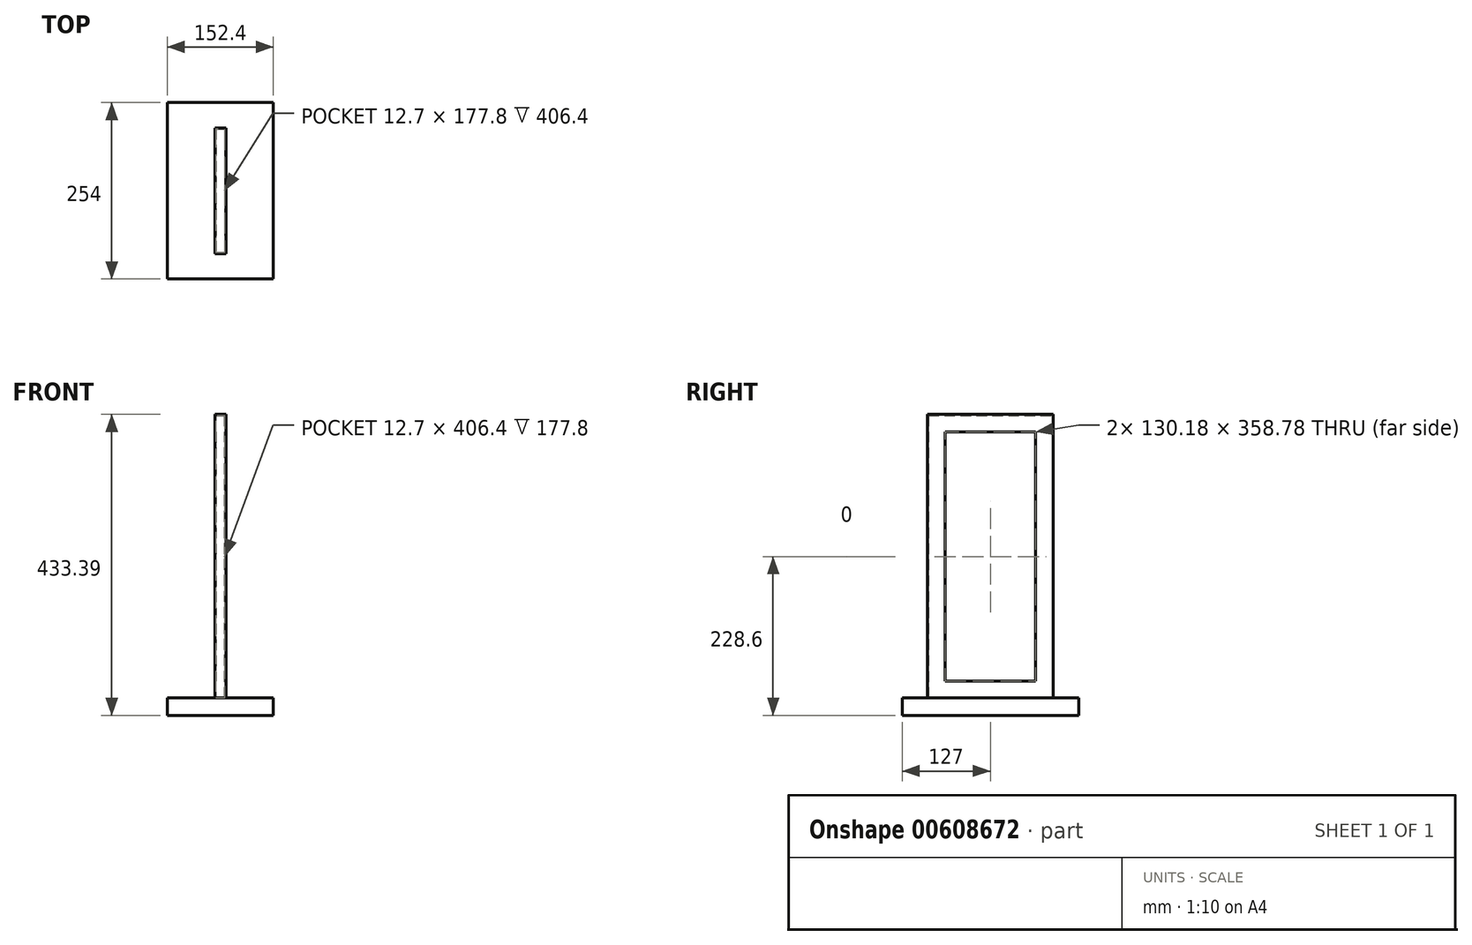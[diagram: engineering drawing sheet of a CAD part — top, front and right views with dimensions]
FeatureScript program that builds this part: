
annotation { "Feature Type Name" : "Feature", "Feature Type Description" : "" }
export const myFeature = defineFeature(function(context is Context, id is Id, definition is map)
    precondition{}
    {
        {
            var Q0;
            Q0=qCreatedBy(makeId("Right.planeOp"),FACE);
            var sketch = newSketch(context, id + "F0", { "sketchPlane" : qUnion([Q0])});
            skPoint(sketch, "E0.middle", {"position": v(0, 228.6) * mm});
            skLineSegment(sketch, "E1.bottom", {"start": v(88.9, 25.4) * mm, "end": v(-88.9, 25.4) * mm});
            skLineSegment(sketch, "E1.top", {"start": v(88.9, 431.8) * mm, "end": v(-88.9, 431.8) * mm});
            skLineSegment(sketch, "E1.left", {"start": v(88.9, 25.4) * mm, "end": v(88.9, 431.8) * mm});
            skLineSegment(sketch, "E1.right", {"start": v(-88.9, 25.4) * mm, "end": v(-88.9, 431.8) * mm});
            skLineSegment(sketch, "E2.bottom", {"start": v(-127, 0) * mm, "end": v(127, 0) * mm});
            skLineSegment(sketch, "E2.top", {"start": v(-127, 25.4) * mm, "end": v(127, 25.4) * mm});
            skLineSegment(sketch, "E2.left", {"start": v(-127, 0) * mm, "end": v(-127, 25.4) * mm});
            skLineSegment(sketch, "E2.right", {"start": v(127, 0) * mm, "end": v(127, 25.4) * mm});
            skPoint(sketch, "E2.middle", {"position": v(0, 12.7) * mm});
            skSolve(sketch);
        }
        {
            var Q0;
            Q0=makeQuery(id+"F0.imprint","IMPRINT",FACE,{"disambiguationData":[TD([[makeQuery(id+"F0.imprint","IMPRINT",EDGE,{"derivedFrom":sQuery(id+"F0.wireOp",EDGE,"E1.top")}),1.0]])]});
            extrude(context, id + "F1", {"entities" : qUnion([Q0]), "endBound" : BoundingType.SYMMETRIC, "depth" : 12.7 * mm, "offsetDistance" : 25.4 * mm});
        }
        {
            var Q0;
            Q0=makeQuery(id+"F0.imprint","IMPRINT",FACE,{"disambiguationData":[TD([[makeQuery(id+"F0.imprint","IMPRINT",EDGE,{"derivedFrom":sQuery(id+"F0.wireOp",EDGE,"E2.bottom")}),1.0]])]});
            extrude(context, id + "F2", {"entities" : qUnion([Q0]), "endBound" : BoundingType.SYMMETRIC, "depth" : 152.4 * mm, "offsetDistance" : 25.4 * mm});
        }
        {
            var Q0;
            Q0=makeQuery(id+"F2.opExtrude","SWEPT_FACE",FACE,{"disambiguationData":[OSD([sQuery(id+"F0.wireOp",EDGE,"E2.top")])]});
            var sketch = newSketch(context, id + "F3", { "sketchPlane" : qUnion([Q0])});
            skLineSegment(sketch, "E3.0.0", {"start": v(-6.35, 88.9) * mm, "end": v(-6.35, -88.9) * mm, "construction": true});
            skLineSegment(sketch, "E3.0.1", {"start": v(-6.35, -88.9) * mm, "end": v(6.35, -88.9) * mm, "construction": true});
            skLineSegment(sketch, "E3.0.2", {"start": v(6.35, -88.9) * mm, "end": v(6.35, 88.9) * mm, "construction": true});
            skLineSegment(sketch, "E3.0.3", {"start": v(6.35, 88.9) * mm, "end": v(-6.35, 88.9) * mm, "construction": true});
            skLineSegment(sketch, "E4", {"start": v(-6.35, -88.9) * mm, "end": v(-6.35, -65.09) * mm});
            skLineSegment(sketch, "E5", {"start": v(-6.35, -65.09) * mm, "end": v(-7.94, -65.09) * mm});
            skLineSegment(sketch, "E6", {"start": v(-7.94, -65.09) * mm, "end": v(-7.94, -90.49) * mm});
            skLineSegment(sketch, "E7", {"start": v(-7.94, -90.49) * mm, "end": v(7.94, -90.49) * mm});
            skLineSegment(sketch, "E8", {"start": v(7.94, -90.49) * mm, "end": v(7.94, -65.09) * mm});
            skLineSegment(sketch, "E9", {"start": v(7.94, -65.09) * mm, "end": v(6.35, -65.09) * mm});
            skLineSegment(sketch, "E10", {"start": v(6.35, -65.09) * mm, "end": v(6.35, -88.9) * mm});
            skLineSegment(sketch, "E11", {"start": v(6.35, -88.9) * mm, "end": v(6.35, 88.9) * mm});
            skLineSegment(sketch, "E12", {"start": v(-6.35, -88.9) * mm, "end": v(6.35, -88.9) * mm});
            skSolve(sketch);
        }
        {
            var Q0;
            Q0=makeQuery(id+"F3.imprint","IMPRINT",FACE,{"disambiguationData":[TD([[makeQuery(id+"F3.imprint","IMPRINT",EDGE,{"derivedFrom":sQuery(id+"F3.wireOp",EDGE,"E4")}),1.0]])]});
            var Q1;
            Q1=makeQuery(id+"F1.opExtrude","CAP_EDGE",EDGE,{"disambiguationData":[OSD([sQuery(id+"F0.wireOp",EDGE,"E1.right")])],"isStart":false});
            var Q2;
            Q2=makeQuery(id+"F1.opExtrude","CAP_EDGE",EDGE,{"disambiguationData":[OSD([sQuery(id+"F0.wireOp",EDGE,"E1.top")])],"isStart":false});
            var Q3;
            Q3=makeQuery(id+"F1.opExtrude","CAP_EDGE",EDGE,{"disambiguationData":[OSD([sQuery(id+"F0.wireOp",EDGE,"E1.left")])],"isStart":false});
            var Q4;
            Q4=sQuery(id+"F3.wireOp",EDGE,"E11");
            sweep(context, id + "F4", {"profiles" : qUnion([Q0]), "path" : qUnion([Q1, Q2, Q3, Q4])});
        }
    });
